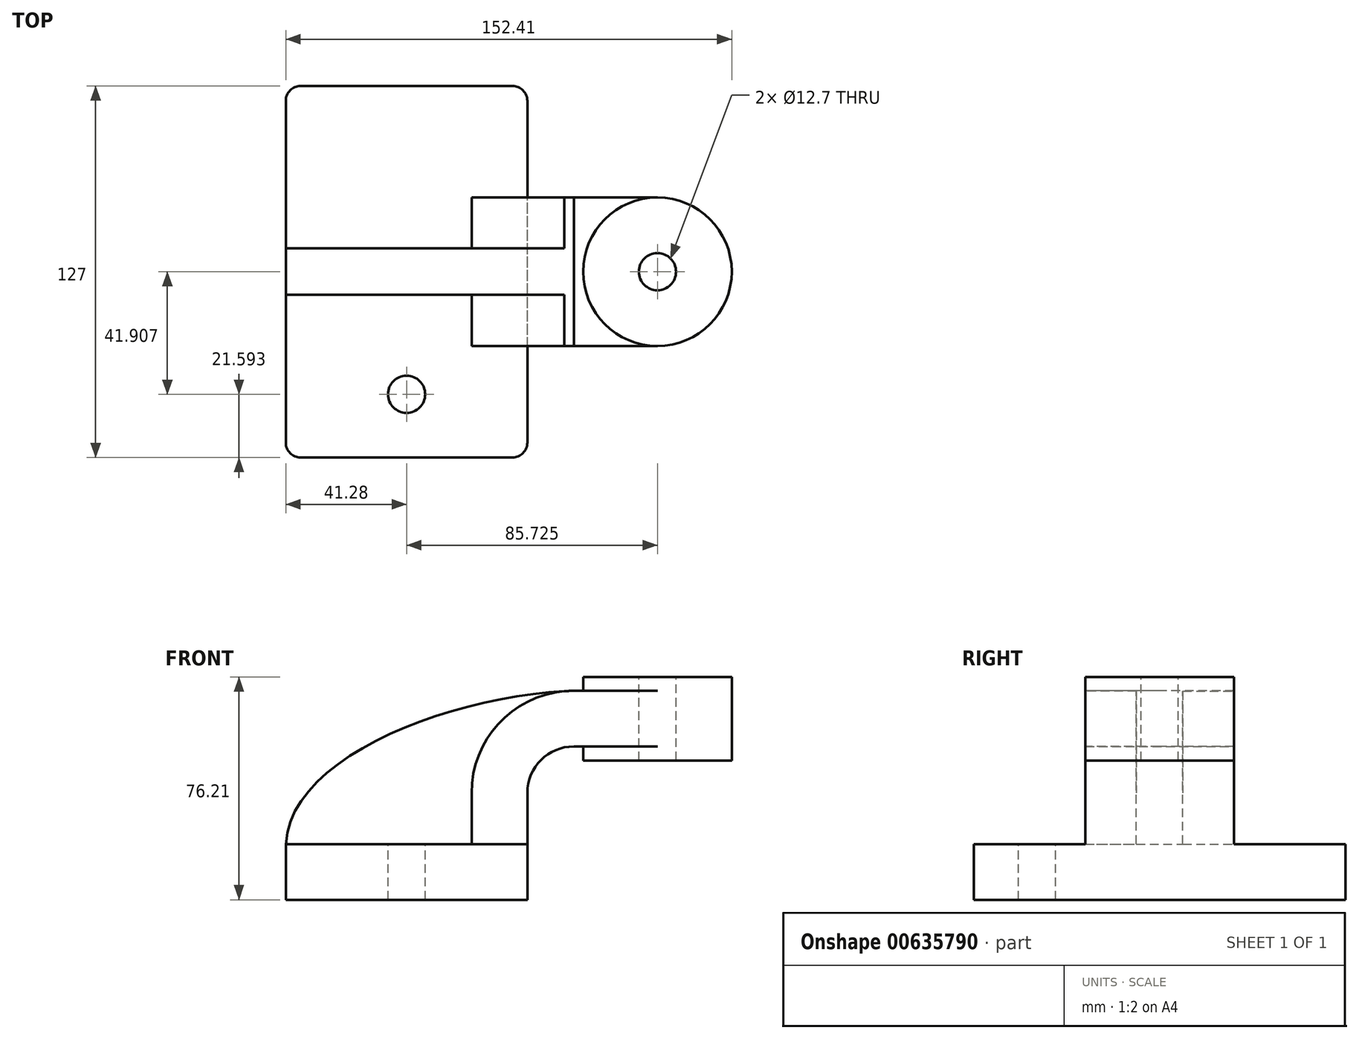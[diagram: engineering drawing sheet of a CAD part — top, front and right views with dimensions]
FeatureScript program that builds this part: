
annotation { "Feature Type Name" : "Feature", "Feature Type Description" : "" }
export const myFeature = defineFeature(function(context is Context, id is Id, definition is map)
    precondition{}
    {
        {
            var Q0;
            Q0=qCreatedBy(makeId("Front.planeOp"),FACE);
            var sketch = newSketch(context, id + "F0", { "sketchPlane" : qUnion([Q0])});
            skLineSegment(sketch, "E0.rect.bottom", {"start": v(-41.28, 9.52) * mm, "end": v(41.28, 9.52) * mm});
            skLineSegment(sketch, "E0.rect.top", {"start": v(-41.28, -9.52) * mm, "end": v(41.28, -9.52) * mm});
            skLineSegment(sketch, "E0.rect.left", {"start": v(-41.28, 9.52) * mm, "end": v(-41.28, -9.52) * mm});
            skLineSegment(sketch, "E0.rect.right", {"start": v(41.28, 9.52) * mm, "end": v(41.28, -9.52) * mm});
            skPoint(sketch, "E0.rect.middle", {"position": v(0, 0) * mm});
            skLineSegment(sketch, "E1", {"start": v(41.28, 9.52) * mm, "end": v(41.28, 27) * mm});
            skArc(sketch, "E2", {"start": v(41.28, 27) * mm, "mid": v(45.92, 38.23) * mm, "end": v(57.15, 42.88) * mm});
            skLineSegment(sketch, "E3", {"start": v(57.15, 42.88) * mm, "end": v(85.72, 42.88) * mm});
            skLineSegment(sketch, "E4.rect.bottom", {"start": v(60.32, 38.1) * mm, "end": v(111.12, 38.1) * mm});
            skLineSegment(sketch, "E4.rect.top", {"start": v(60.32, 66.68) * mm, "end": v(111.12, 66.68) * mm});
            skLineSegment(sketch, "E4.rect.left", {"start": v(60.32, 38.1) * mm, "end": v(60.32, 66.68) * mm});
            skLineSegment(sketch, "E4.rect.right", {"start": v(111.13, 38.1) * mm, "end": v(111.12, 66.68) * mm});
            skPoint(sketch, "E4.rect.middle", {"position": v(85.72, 52.39) * mm});
            skLineSegment(sketch, "E5.0", {"start": v(57.15, 61.93) * mm, "end": v(85.72, 61.93) * mm});
            skArc(sketch, "E5.1", {"start": v(22.23, 27) * mm, "mid": v(32.45, 51.7) * mm, "end": v(57.15, 61.93) * mm});
            skLineSegment(sketch, "E5.2", {"start": v(22.23, 9.52) * mm, "end": v(22.23, 27) * mm});
            skLineSegment(sketch, "E6", {"start": v(85.72, 38.1) * mm, "end": v(85.72, 66.68) * mm});
            skFitSpline(sketch, "E7", {"points": [v(-41.28, 9.53) * mm, v(57.15, 61.93) * mm], "startDerivative": vector(5.2, 92.34) * mm, "endDerivative": vector(120.92, 4.22) * mm});
            skSolve(sketch);
        }
        {
            var Q0;
            Q0=makeQuery(id+"F0.imprint","IMPRINT",FACE,{"disambiguationData":[TD([[makeQuery(id+"F0.imprint","IMPRINT",EDGE,{"derivedFrom":sQuery(id+"F0.wireOp",EDGE,"E0.rect.top")}),1.0]])]});
            extrude(context, id + "F1", {"entities" : qUnion([Q0]), "endBound" : BoundingType.SYMMETRIC, "depth" : 127 * mm});
        }
        {
            var Q0;
            {var subQ9=sQuery(id+"F0.wireOp",EDGE,"E1");Q0=makeQuery(id+"F0.imprint","IMPRINT",FACE,{"disambiguationData":[TD([[makeQuery(id+"F0.imprint","IMPRINT",EDGE,{"derivedFrom":subQ9}),1.0]])]});}
            var Q1;
            {var subQ0=sQuery(id+"F0.wireOp",EDGE,"E6");var subQ1=sQuery(id+"F0.wireOp",EDGE,"E3");var subQ2=makeQuery(id+"F0.imprint","INTERSECT",VERTEX,{"derivedFrom":[subQ1,subQ0]});Q1=makeQuery(id+"F0.imprint","IMPRINT",FACE,{"disambiguationData":[TD([[makeQuery(id+"F0.imprint","IMPRINT",EDGE,{"disambiguationData":[TD([[subQ2,1.0]])],"derivedFrom":subQ1}),1.0]])]});}
            extrude(context, id + "F2", {"entities" : qUnion([Q0, Q1]), "operationType" : NewBodyOperationType.ADD, "endBound" : BoundingType.SYMMETRIC, "depth" : 50.8 * mm});
        }
        {
            var Q0;
            {var subQ3=sQuery(id+"F0.wireOp",EDGE,"E5.2");Q0=makeQuery(id+"F0.imprint","IMPRINT",FACE,{"disambiguationData":[TD([[makeQuery(id+"F0.imprint","IMPRINT",EDGE,{"derivedFrom":subQ3}),1.0]])]});}
            extrude(context, id + "F3", {"entities" : qUnion([Q0]), "operationType" : NewBodyOperationType.ADD, "endBound" : BoundingType.SYMMETRIC, "depth" : 15.88 * mm});
        }
        {
            var Q0;
            {var subQ5=sQuery(id+"F0.wireOp",EDGE,"E4.rect.right");Q0=makeQuery(id+"F0.imprint","IMPRINT",FACE,{"disambiguationData":[TD([[makeQuery(id+"F0.imprint","IMPRINT",EDGE,{"derivedFrom":subQ5}),1.0]])]});}
            var Q1;
            Q1=sQuery(id+"F0.wireOp",EDGE,"E6");
            revolve(context, id + "F4", {"operationType" : NewBodyOperationType.ADD, "entities" : qUnion([Q0]), "axis" : qUnion([Q1]), "revolveType" : RevolveType.FULL});
        }
        {
            var Q0;
            Q0=makeQuery(id+"F1.opExtrude","CAP_EDGE",EDGE,{"disambiguationData":[OSD([sQuery(id+"F0.wireOp",EDGE,"E0.rect.right")])],"isStart":false});
            var Q1;
            Q1=makeQuery(id+"F1.opExtrude","CAP_EDGE",EDGE,{"disambiguationData":[OSD([sQuery(id+"F0.wireOp",EDGE,"E0.rect.left")])],"isStart":false});
            var Q2;
            Q2=makeQuery(id+"F1.opExtrude","CAP_EDGE",EDGE,{"disambiguationData":[OSD([sQuery(id+"F0.wireOp",EDGE,"E0.rect.right")])],"isStart":true});
            var Q3;
            Q3=makeQuery(id+"F1.opExtrude","CAP_EDGE",EDGE,{"disambiguationData":[OSD([sQuery(id+"F0.wireOp",EDGE,"E0.rect.left")])],"isStart":true});
            fillet(context, id + "F5", {"entities" : qUnion([Q0, Q1, Q2, Q3]), "radius" : 5.08 * mm, "tangentPropagation" : true, "allowEdgeOverflow" : false});
        }
        {
            var Q0;
            Q0=makeQuery(id+"F4.opRevolve","SWEPT_FACE",FACE,{"disambiguationData":[OSD([sQuery(id+"F0.wireOp",EDGE,"E4.rect.top")])]});
            var sketch = newSketch(context, id + "F6", { "sketchPlane" : qUnion([Q0])});
            skCircle(sketch, "E8", {"center": v(85.72, 0) * mm, "radius": 6.35 * mm});
            skSolve(sketch);
        }
        {
            var Q0;
            Q0=makeQuery(id+"F4.opRevolve","SWEPT_FACE",FACE,{"disambiguationData":[OSD([sQuery(id+"F0.wireOp",EDGE,"E4.rect.bottom")])]});
            var sketch = newSketch(context, id + "F7", { "sketchPlane" : qUnion([Q0])});
            skCircle(sketch, "E9", {"center": v(85.72, 0) * mm, "radius": 10.89 * mm});
            skSolve(sketch);
        }
        {
            var Q0;
            Q0=sQuery(id+"F6.wireOp",VERTEX,"E8.center");
            var Q1;
            Q1=sQuery(id+"F7.wireOp",VERTEX,"E9.center");
            var Q2;
            Q2=makeQuery(id+"F1.opExtrude","SWEPT_BODY",BODY,{"disambiguationData":[OSD([sQuery(id+"F0.wireOp",EDGE,"E0.rect.bottom"),sQuery(id+"F0.wireOp",EDGE,"E0.rect.top"),sQuery(id+"F0.wireOp",EDGE,"E0.rect.left"),sQuery(id+"F0.wireOp",EDGE,"E0.rect.right")])]});
            hole(context, id + "F8", {"style" : HoleStyle.SIMPLE, "endStyle" : HoleEndStyle.THROUGH, "holeDiameter" : 12.7 * mm, "majorDiameter" : 6.35 * mm, "isTappedThrough" : true, "tappedDepth" : 12.7 * mm, "tapClearance" : 3, "locations" : qUnion([Q0, Q1]), "scope" : qUnion([Q2])});
        }
        {
            var Q0;
            {var subQ4=sQuery(id+"F0.wireOp",EDGE,"E0.rect.bottom");var subQ5=sQuery(id+"F0.wireOp",EDGE,"E0.rect.right");var subQ6=sQuery(id+"F0.wireOp",EDGE,"E0.rect.left");Q0=makeQuery(id+"F3.boolean.opBoolean","SPLIT",FACE,{"disambiguationData":[TD([makeQuery(id+"F1.opExtrude","CAP_FACE",FACE,{"disambiguationData":[OSD([subQ4,sQuery(id+"F0.wireOp",EDGE,"E0.rect.top"),subQ6,subQ5])],"isStart":false})])],"derivedFrom":makeQuery(id+"F1.opExtrude","SWEPT_FACE",FACE,{"disambiguationData":[OSD([subQ4])]})});}
            var sketch = newSketch(context, id + "F9", { "sketchPlane" : qUnion([Q0])});
            skLineSegment(sketch, "E10.0", {"start": v(-36.2, -63.5) * mm, "end": v(36.2, -63.5) * mm, "construction": true});
            skLineSegment(sketch, "E11", {"start": v(0, -63.5) * mm, "end": v(0, -41.9) * mm, "construction": true});
            skPoint(sketch, "E11.endSnap0", {"position": v(0, -63.5) * mm});
            skSolve(sketch);
        }
        {
            var Q0;
            Q0=sQuery(id+"F9.wireOp",VERTEX,"E11.end");
            var Q1;
            Q1=makeQuery(id+"F1.opExtrude","SWEPT_BODY",BODY,{"disambiguationData":[OSD([sQuery(id+"F0.wireOp",EDGE,"E0.rect.bottom"),sQuery(id+"F0.wireOp",EDGE,"E0.rect.top"),sQuery(id+"F0.wireOp",EDGE,"E0.rect.left"),sQuery(id+"F0.wireOp",EDGE,"E0.rect.right")])]});
            hole(context, id + "F10", {"style" : HoleStyle.SIMPLE, "endStyle" : HoleEndStyle.THROUGH, "holeDiameter" : 12.7 * mm, "majorDiameter" : 6.35 * mm, "isTappedThrough" : true, "tappedDepth" : 12.7 * mm, "tapClearance" : 3, "locations" : qUnion([Q0]), "scope" : qUnion([Q1])});
        }
    });
